# Revit family: WA-1000-1500
name_source: partatom
category: Generic Models
revit_build: Autodesk Revit 2017 (Build: 20171027_0315(x64)
units: mm (PartAtom-declared; Revit-internal decimal feet)

## family parameters
Always vertical = Yes
Can host rebar = No
Cut with Voids When Loaded = No
Host = Floor
Part Type = Normal
Room Calculation Point = No
Round Connector Dimension = Use Diameter
Shared = Yes

## types (5) — shared parameters
Belastbaarheid = 15 kN/m² volgens NEN-EN1991
Bevestiging = Verankering opgenomen in vormgeving frame
C = 400 mm  [stored 1.31234 ft]
Model = WA
Speciale afmeting = > 1000 x 2500 met 2 deksels (D = 2 deksels)
URL = https://www.gortergroup.com
frame = geanodiseerd aluminium frame
rubber = <By Category>
vloerluik = geanodiseerd aluminium traanplaat

## per-type parameters (varying)
| type | A | B | Weight (kg) |
| WA-600-600 | 600 mm | 600 mm | 19 |
| WA-800-800 | 800 mm  [stored 2.62467 ft] | 800 mm  [stored 2.62467 ft] | 28 |
| WA-1000-1000 | 1000 mm  [stored 3.28084 ft] | 1000 mm  [stored 3.28084 ft] | 36 |
| WA-1000-2000 | 2000 mm  [stored 6.56168 ft] | 1000 mm  [stored 3.28084 ft] | 65 |
| WA-1000-1500 | 1500 mm  [stored 4.92126 ft] | 1000 mm  [stored 3.28084 ft] | 52 |

note: [stored X ft] marks values corroborated as IEEE doubles in the binary element streams (Revit-internal decimal feet)

## geometry (parser evidence)
native form markers: Sweep x7
no freeform markers — native parametric forms only
